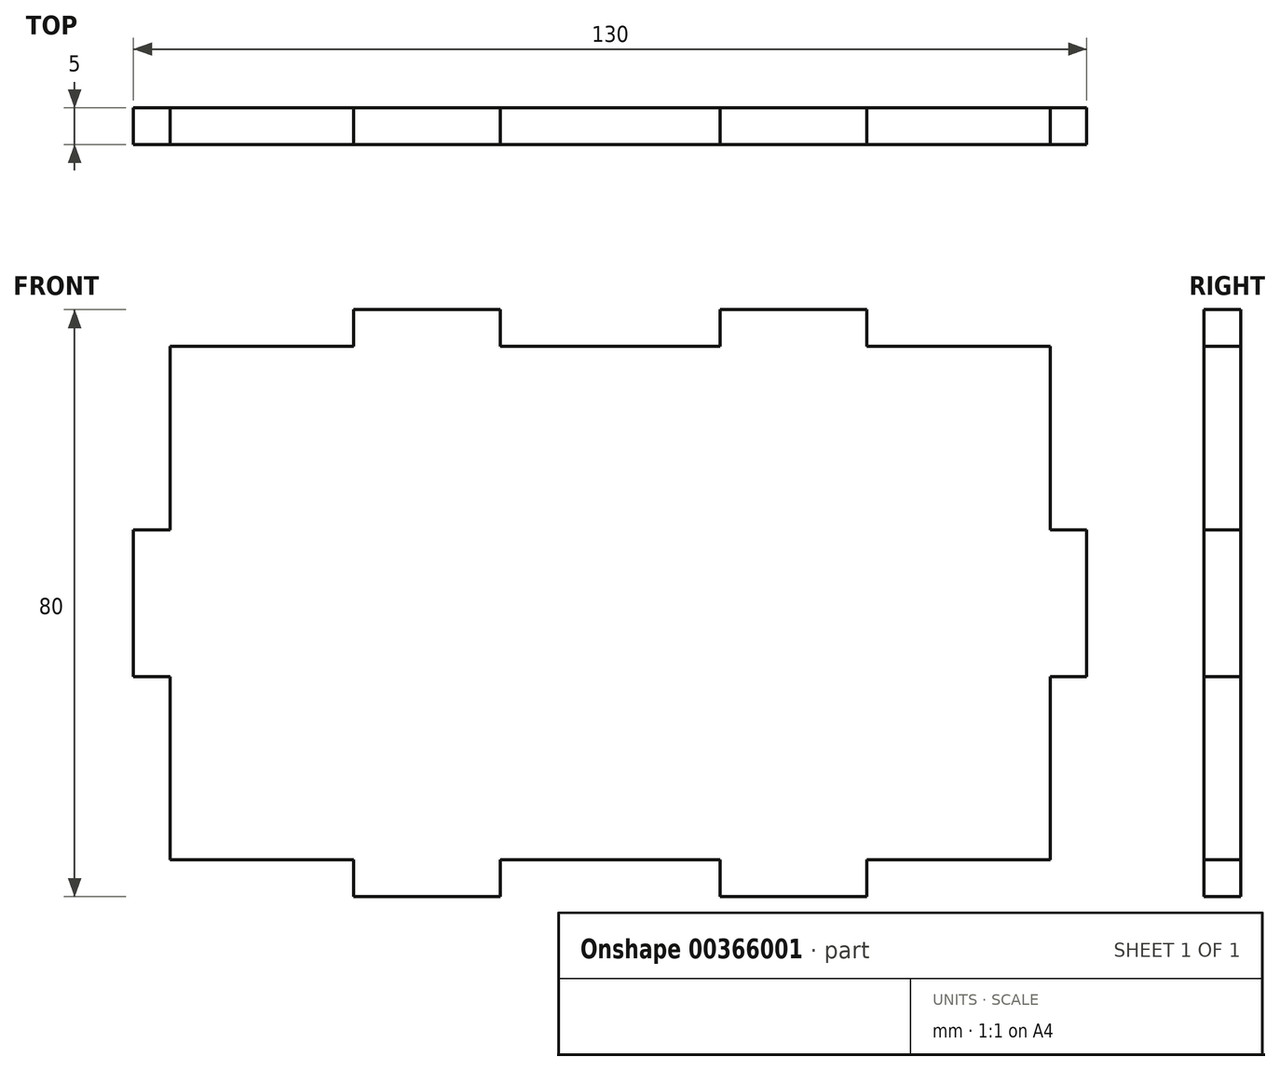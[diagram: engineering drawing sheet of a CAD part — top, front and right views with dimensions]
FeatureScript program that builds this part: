
annotation { "Feature Type Name" : "Feature", "Feature Type Description" : "" }
export const myFeature = defineFeature(function(context is Context, id is Id, definition is map)
    precondition{}
    {
        {
            var Q0;
            Q0=qCreatedBy(makeId("Front.planeOp"),FACE);
            var sketch = newSketch(context, id + "F0", { "sketchPlane" : qUnion([Q0])});
            skLineSegment(sketch, "E0", {"start": v(0, 0) * mm, "end": v(25, 0) * mm});
            skLineSegment(sketch, "E1", {"start": v(25, 0) * mm, "end": v(25, -5) * mm});
            skLineSegment(sketch, "E2", {"start": v(25, -5) * mm, "end": v(45, -5) * mm});
            skLineSegment(sketch, "E3", {"start": v(45, -5) * mm, "end": v(45, 0) * mm});
            skLineSegment(sketch, "E4", {"start": v(45, 0) * mm, "end": v(75, 0) * mm});
            skLineSegment(sketch, "E5", {"start": v(75, 0) * mm, "end": v(75, -5) * mm});
            skLineSegment(sketch, "E6", {"start": v(75, -5) * mm, "end": v(95, -5) * mm});
            skLineSegment(sketch, "E7", {"start": v(95, -5) * mm, "end": v(95, 0) * mm});
            skLineSegment(sketch, "E8", {"start": v(95, 0) * mm, "end": v(120, 0) * mm});
            skLineSegment(sketch, "E9", {"start": v(120, 0) * mm, "end": v(120, 25) * mm});
            skLineSegment(sketch, "E10", {"start": v(120, 25) * mm, "end": v(125, 25) * mm});
            skLineSegment(sketch, "E11", {"start": v(125, 25) * mm, "end": v(125, 45) * mm});
            skLineSegment(sketch, "E12", {"start": v(125, 45) * mm, "end": v(120, 45) * mm});
            skLineSegment(sketch, "E13", {"start": v(120, 45) * mm, "end": v(120, 70) * mm});
            skLineSegment(sketch, "E14", {"start": v(120, 70) * mm, "end": v(95, 70) * mm});
            skLineSegment(sketch, "E15", {"start": v(95, 70) * mm, "end": v(95, 75) * mm});
            skLineSegment(sketch, "E16", {"start": v(95, 75) * mm, "end": v(75, 75) * mm});
            skLineSegment(sketch, "E17", {"start": v(75, 75) * mm, "end": v(75, 70) * mm});
            skLineSegment(sketch, "E18", {"start": v(75, 70) * mm, "end": v(45, 70) * mm});
            skLineSegment(sketch, "E19", {"start": v(45, 70) * mm, "end": v(45, 75) * mm});
            skLineSegment(sketch, "E20", {"start": v(45, 75) * mm, "end": v(25, 75) * mm});
            skLineSegment(sketch, "E21", {"start": v(25, 75) * mm, "end": v(25, 70) * mm});
            skLineSegment(sketch, "E22", {"start": v(25, 70) * mm, "end": v(0, 70) * mm});
            skLineSegment(sketch, "E23", {"start": v(0, 70) * mm, "end": v(0, 45) * mm});
            skLineSegment(sketch, "E24", {"start": v(0, 45) * mm, "end": v(-5, 45) * mm});
            skLineSegment(sketch, "E25", {"start": v(-5, 45) * mm, "end": v(-5, 25) * mm});
            skLineSegment(sketch, "E26", {"start": v(-5, 25) * mm, "end": v(0, 25) * mm});
            skLineSegment(sketch, "E27", {"start": v(0, 25) * mm, "end": v(0, 0) * mm});
            skSolve(sketch);
        }
        {
            var Q0;
            Q0=makeQuery(id+"F0.imprint","IMPRINT",FACE,{"disambiguationData":[TD([[makeQuery(id+"F0.imprint","IMPRINT",EDGE,{"derivedFrom":sQuery(id+"F0.wireOp",EDGE,"E0")}),1.0]])]});
            extrude(context, id + "F1", {"entities" : qUnion([Q0]), "depth" : 5 * mm});
        }
    });
